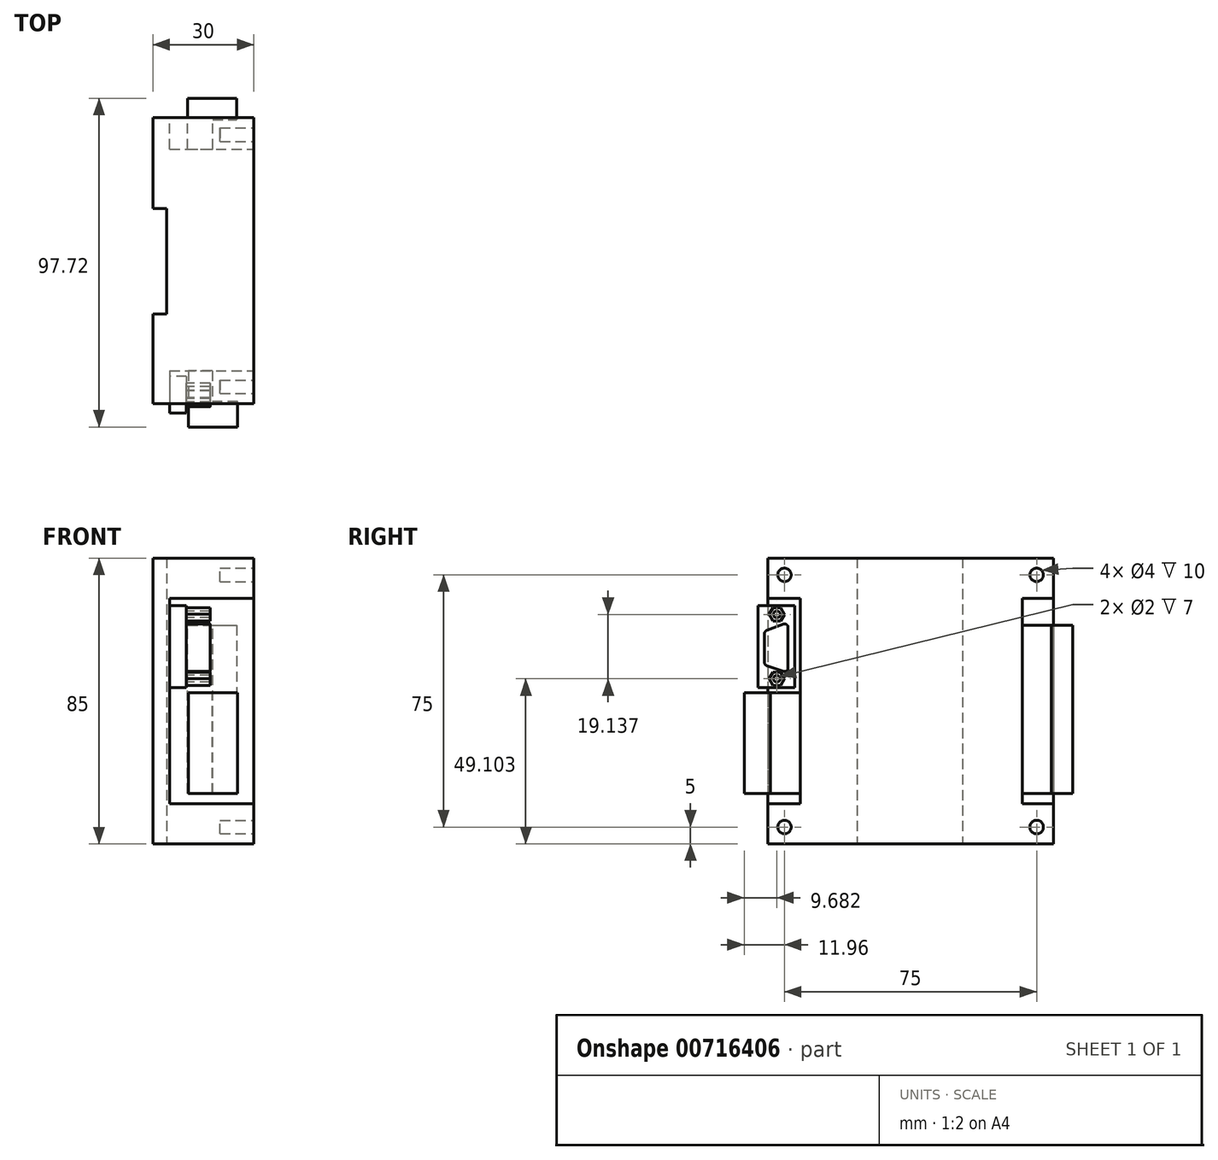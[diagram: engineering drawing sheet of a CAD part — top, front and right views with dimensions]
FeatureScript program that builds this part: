
annotation { "Feature Type Name" : "Feature", "Feature Type Description" : "" }
export const myFeature = defineFeature(function(context is Context, id is Id, definition is map)
    precondition{}
    {
        {
            var Q0;
            Q0=qCreatedBy(makeId("Top.planeOp"),FACE);
            var sketch = newSketch(context, id + "F0", { "sketchPlane" : qUnion([Q0])});
            skLineSegment(sketch, "E0.bottom", {"start": v(-15, 42.5) * mm, "end": v(15, 42.5) * mm});
            skLineSegment(sketch, "E0.top", {"start": v(-15, -42.5) * mm, "end": v(15, -42.5) * mm});
            skLineSegment(sketch, "E0.left", {"start": v(-15, 42.5) * mm, "end": v(-15, 15.5) * mm});
            skLineSegment(sketch, "E0.right", {"start": v(15, 42.5) * mm, "end": v(15, -42.5) * mm});
            skPoint(sketch, "E0.middle", {"position": v(0, 0) * mm});
            skLineSegment(sketch, "E1", {"start": v(-15, -15.87) * mm, "end": v(-10.94, -15.87) * mm});
            skLineSegment(sketch, "E2", {"start": v(-10.94, -15.87) * mm, "end": v(-10.94, 15.5) * mm});
            skLineSegment(sketch, "E3", {"start": v(-10.94, 15.5) * mm, "end": v(-15, 15.5) * mm});
            skLineSegment(sketch, "E4.trimOffspring", {"start": v(-15, -15.87) * mm, "end": v(-15, -42.5) * mm});
            skSolve(sketch);
        }
        {
            var Q0;
            Q0 = qSketchRegion(id + "F0", true);
            extrude(context, id + "F1", {"entities" : qUnion([Q0]), "depth" : 85 * mm, "offsetDistance" : 25 * mm});
        }
        {
            var Q0;
            Q0=makeQuery(id+"F1.opExtrude","SWEPT_FACE",FACE,{"disambiguationData":[OSD([sQuery(id+"F0.wireOp",EDGE,"E0.right")])]});
            var sketch = newSketch(context, id + "F2", { "sketchPlane" : qUnion([Q0])});
            skCircle(sketch, "E5", {"center": v(-37.5, 5) * mm, "radius": 2 * mm});
            skCircle(sketch, "E6.MirrorC", {"center": v(37.5, 5) * mm, "radius": 2 * mm});
            skLineSegment(sketch, "E7", {"start": v(-42.5, 42.5) * mm, "end": v(42.5, 42.5) * mm, "construction": true});
            skCircle(sketch, "E8.MirrorC", {"center": v(37.5, 80) * mm, "radius": 2 * mm});
            skCircle(sketch, "E9.MirrorC", {"center": v(-37.5, 80) * mm, "radius": 2 * mm});
            skSolve(sketch);
        }
        {
            var Q0;
            Q0 = qSketchRegion(id + "F2", true);
            extrude(context, id + "F3", {"entities" : qUnion([Q0]), "operationType" : NewBodyOperationType.REMOVE, "oppositeDirection" : true, "depth" : 10 * mm, "offsetDistance" : 25 * mm});
        }
        {
            var Q0;
            Q0=makeQuery(id+"F1.opExtrude","SWEPT_FACE",FACE,{"disambiguationData":[OSD([sQuery(id+"F0.wireOp",EDGE,"E0.right")])]});
            var sketch = newSketch(context, id + "F4", { "sketchPlane" : qUnion([Q0])});
            skLineSegment(sketch, "E10.bottom", {"start": v(-32.76, 73.03) * mm, "end": v(-52.24, 73.03) * mm});
            skLineSegment(sketch, "E10.top", {"start": v(-32.76, 11.97) * mm, "end": v(-52.24, 11.97) * mm});
            skLineSegment(sketch, "E10.left", {"start": v(-32.76, 73.03) * mm, "end": v(-32.76, 11.97) * mm});
            skLineSegment(sketch, "E10.right", {"start": v(-52.24, 73.03) * mm, "end": v(-52.24, 11.97) * mm});
            skPoint(sketch, "E10.middle", {"position": v(-42.5, 42.5) * mm});
            skLineSegment(sketch, "E11.bottom", {"start": v(33.22, 11.97) * mm, "end": v(51.78, 11.97) * mm});
            skLineSegment(sketch, "E11.top", {"start": v(33.22, 73.03) * mm, "end": v(51.78, 73.03) * mm});
            skLineSegment(sketch, "E11.left", {"start": v(33.22, 11.97) * mm, "end": v(33.22, 73.03) * mm});
            skLineSegment(sketch, "E11.right", {"start": v(51.78, 11.97) * mm, "end": v(51.78, 73.03) * mm});
            skPoint(sketch, "E11.middle", {"position": v(42.5, 42.5) * mm});
            skSolve(sketch);
        }
        {
            var Q0;
            Q0 = qSketchRegion(id + "F4", true);
            extrude(context, id + "F5", {"entities" : qUnion([Q0]), "operationType" : NewBodyOperationType.REMOVE, "oppositeDirection" : true, "depth" : 25 * mm, "offsetDistance" : 25 * mm});
        }
        {
            var Q0;
            Q0=qCreatedBy(makeId("Top.planeOp"),FACE);
            cPlane(context, id + "F6", {"entities" : qUnion([Q0]), "cplaneType" : CPlaneType.OFFSET, "offset" : 15 * mm, "width" : 150 * mm, "height" : 150 * mm});
        }
        {
            var Q0;
            Q0=qCreatedBy(id+"F6.planeOp",FACE);
            var sketch = newSketch(context, id + "F7", { "sketchPlane" : qUnion([Q0])});
            skLineSegment(sketch, "E12.bottom", {"start": v(-4.64, 33.03) * mm, "end": v(2.82, 33.03) * mm});
            skLineSegment(sketch, "E12.top", {"start": v(-4.64, 48.26) * mm, "end": v(2.82, 48.26) * mm});
            skLineSegment(sketch, "E12.left", {"start": v(-4.64, 33.03) * mm, "end": v(-4.64, 48.26) * mm});
            skLineSegment(sketch, "E12.right", {"start": v(2.82, 33.03) * mm, "end": v(2.82, 41.92) * mm});
            skLineSegment(sketch, "E13.bottom", {"start": v(2.82, 48.26) * mm, "end": v(9.94, 48.26) * mm});
            skLineSegment(sketch, "E13.top", {"start": v(2.82, 41.92) * mm, "end": v(9.94, 41.92) * mm});
            skLineSegment(sketch, "E13.right", {"start": v(9.94, 48.26) * mm, "end": v(9.94, 41.92) * mm});
            skSolve(sketch);
        }
        {
            var Q0;
            Q0 = qSketchRegion(id + "F7", true);
            extrude(context, id + "F8", {"entities" : qUnion([Q0]), "operationType" : NewBodyOperationType.ADD, "depth" : 50 * mm, "offsetDistance" : 25 * mm});
        }
        {
            var Q0;
            Q0=qCreatedBy(id+"F6.planeOp",FACE);
            var sketch = newSketch(context, id + "F9", { "sketchPlane" : qUnion([Q0])});
            skLineSegment(sketch, "E14.bottom", {"start": v(-4.44, -32.5) * mm, "end": v(2.64, -32.5) * mm});
            skLineSegment(sketch, "E14.top", {"start": v(-4.44, -49.46) * mm, "end": v(2.64, -49.46) * mm});
            skLineSegment(sketch, "E14.left", {"start": v(-4.44, -32.5) * mm, "end": v(-4.44, -49.46) * mm});
            skLineSegment(sketch, "E14.right", {"start": v(2.64, -32.5) * mm, "end": v(2.64, -41.75) * mm});
            skLineSegment(sketch, "E15.bottom", {"start": v(2.64, -49.46) * mm, "end": v(10.17, -49.46) * mm});
            skLineSegment(sketch, "E15.top", {"start": v(2.64, -41.75) * mm, "end": v(10.17, -41.75) * mm});
            skLineSegment(sketch, "E15.right", {"start": v(10.17, -49.46) * mm, "end": v(10.17, -41.75) * mm});
            skSolve(sketch);
        }
        {
            var Q0;
            Q0 = qSketchRegion(id + "F9", true);
            extrude(context, id + "F10", {"entities" : qUnion([Q0]), "operationType" : NewBodyOperationType.ADD, "depth" : 30 * mm, "offsetDistance" : 25 * mm});
        }
        {
            var Q0;
            Q0=makeQuery(id+"F5.boolean.opBoolean","COPY",FACE,{"derivedFrom":makeQuery(id+"F5.opExtrude","CAP_FACE",FACE,{"disambiguationData":[OSD([sQuery(id+"F4.wireOp",EDGE,"E10.bottom"),sQuery(id+"F4.wireOp",EDGE,"E10.top"),sQuery(id+"F4.wireOp",EDGE,"E10.left"),sQuery(id+"F4.wireOp",EDGE,"E10.right")])],"isStart":false})});
            var sketch = newSketch(context, id + "F11", { "sketchPlane" : qUnion([Q0])});
            skLineSegment(sketch, "E16.bottom", {"start": v(-34.45, 70.86) * mm, "end": v(-45.32, 70.86) * mm});
            skLineSegment(sketch, "E16.top", {"start": v(-34.45, 46.5) * mm, "end": v(-45.32, 46.5) * mm});
            skLineSegment(sketch, "E16.left", {"start": v(-34.45, 70.86) * mm, "end": v(-34.45, 46.5) * mm});
            skLineSegment(sketch, "E16.right", {"start": v(-45.32, 70.86) * mm, "end": v(-45.32, 46.5) * mm});
            skSolve(sketch);
        }
        {
            var Q0;
            Q0 = qSketchRegion(id + "F11", true);
            extrude(context, id + "F12", {"entities" : qUnion([Q0]), "operationType" : NewBodyOperationType.ADD, "depth" : 5 * mm, "offsetDistance" : 25 * mm});
        }
        {
            var Q0;
            Q0=makeQuery(id+"F12.opExtrude","CAP_FACE",FACE,{"disambiguationData":[OSD([sQuery(id+"F11.wireOp",EDGE,"E16.bottom"),sQuery(id+"F11.wireOp",EDGE,"E16.top"),sQuery(id+"F11.wireOp",EDGE,"E16.left"),sQuery(id+"F11.wireOp",EDGE,"E16.right")])],"isStart":false});
            var sketch = newSketch(context, id + "F13", { "sketchPlane" : qUnion([Q0])});
            skLineSegment(sketch, "E17", {"start": v(-36.45, 64.41) * mm, "end": v(-36.45, 52.25) * mm});
            skLineSegment(sketch, "E18", {"start": v(-37.77, 51.3) * mm, "end": v(-42.77, 53) * mm});
            skLineSegment(sketch, "E19", {"start": v(-43.45, 53.94) * mm, "end": v(-43.45, 62.53) * mm});
            skLineSegment(sketch, "E20", {"start": v(-42.8, 63.47) * mm, "end": v(-37.8, 65.35) * mm});
            skCircle(sketch, "E21", {"center": v(-39.78, 68.24) * mm, "radius": 1 * mm});
            skCircle(sketch, "E22", {"center": v(-39.78, 49.1) * mm, "radius": 1 * mm});
            skPoint(sketch, "E23.visualSharp", {"position": v(-36.45, 65.86) * mm});
            skArc(sketch, "E23.filletArc", {"start": v(-36.45, 64.41) * mm, "mid": v(-36.88, 65.23) * mm, "end": v(-37.8, 65.35) * mm});
            skPoint(sketch, "E24.visualSharp", {"position": v(-36.45, 50.86) * mm});
            skArc(sketch, "E24.filletArc", {"start": v(-37.77, 51.3) * mm, "mid": v(-36.87, 51.44) * mm, "end": v(-36.45, 52.25) * mm});
            skPoint(sketch, "E25.visualSharp", {"position": v(-43.45, 63.22) * mm});
            skArc(sketch, "E25.filletArc", {"start": v(-42.8, 63.47) * mm, "mid": v(-43.27, 63.1) * mm, "end": v(-43.45, 62.53) * mm});
            skPoint(sketch, "E26.visualSharp", {"position": v(-43.45, 53.22) * mm});
            skArc(sketch, "E26.filletArc", {"start": v(-43.45, 53.94) * mm, "mid": v(-43.26, 53.36) * mm, "end": v(-42.77, 53) * mm});
            skCircle(sketch, "E27.cCircle", {"center": v(-39.78, 68.24) * mm, "radius": 2 * mm, "construction": true});
            skLineSegment(sketch, "E27.0", {"start": v(-40.96, 66.25) * mm, "end": v(-42.09, 68.27) * mm});
            skLineSegment(sketch, "E27.1", {"start": v(-42.09, 68.27) * mm, "end": v(-40.9, 70.25) * mm});
            skLineSegment(sketch, "E27.2", {"start": v(-40.9, 70.25) * mm, "end": v(-38.6, 70.23) * mm});
            skLineSegment(sketch, "E27.3", {"start": v(-38.6, 70.23) * mm, "end": v(-37.47, 68.21) * mm});
            skLineSegment(sketch, "E27.4", {"start": v(-37.47, 68.21) * mm, "end": v(-38.65, 66.23) * mm});
            skLineSegment(sketch, "E27.5", {"start": v(-38.65, 66.23) * mm, "end": v(-40.96, 66.25) * mm});
            skPoint(sketch, "E27.0.midPoint", {"position": v(-41.52, 67.26) * mm});
            skCircle(sketch, "E28.cCircle", {"center": v(-39.78, 49.1) * mm, "radius": 2 * mm, "construction": true});
            skLineSegment(sketch, "E28.0", {"start": v(-40.93, 47.1) * mm, "end": v(-42.09, 49.1) * mm});
            skLineSegment(sketch, "E28.1", {"start": v(-42.09, 49.1) * mm, "end": v(-40.94, 51.1) * mm});
            skLineSegment(sketch, "E28.2", {"start": v(-40.94, 51.1) * mm, "end": v(-38.63, 51.1) * mm});
            skLineSegment(sketch, "E28.3", {"start": v(-38.63, 51.1) * mm, "end": v(-37.47, 49.1) * mm});
            skLineSegment(sketch, "E28.4", {"start": v(-37.47, 49.1) * mm, "end": v(-38.62, 47.1) * mm});
            skLineSegment(sketch, "E28.5", {"start": v(-38.62, 47.1) * mm, "end": v(-40.93, 47.1) * mm});
            skPoint(sketch, "E28.0.midPoint", {"position": v(-41.5, 48.1) * mm});
            skSolve(sketch);
        }
        {
            var Q0;
            Q0 = qSketchRegion(id + "F13", true);
            extrude(context, id + "F14", {"entities" : qUnion([Q0]), "operationType" : NewBodyOperationType.ADD, "depth" : 7 * mm, "offsetDistance" : 25 * mm});
        }
    });
